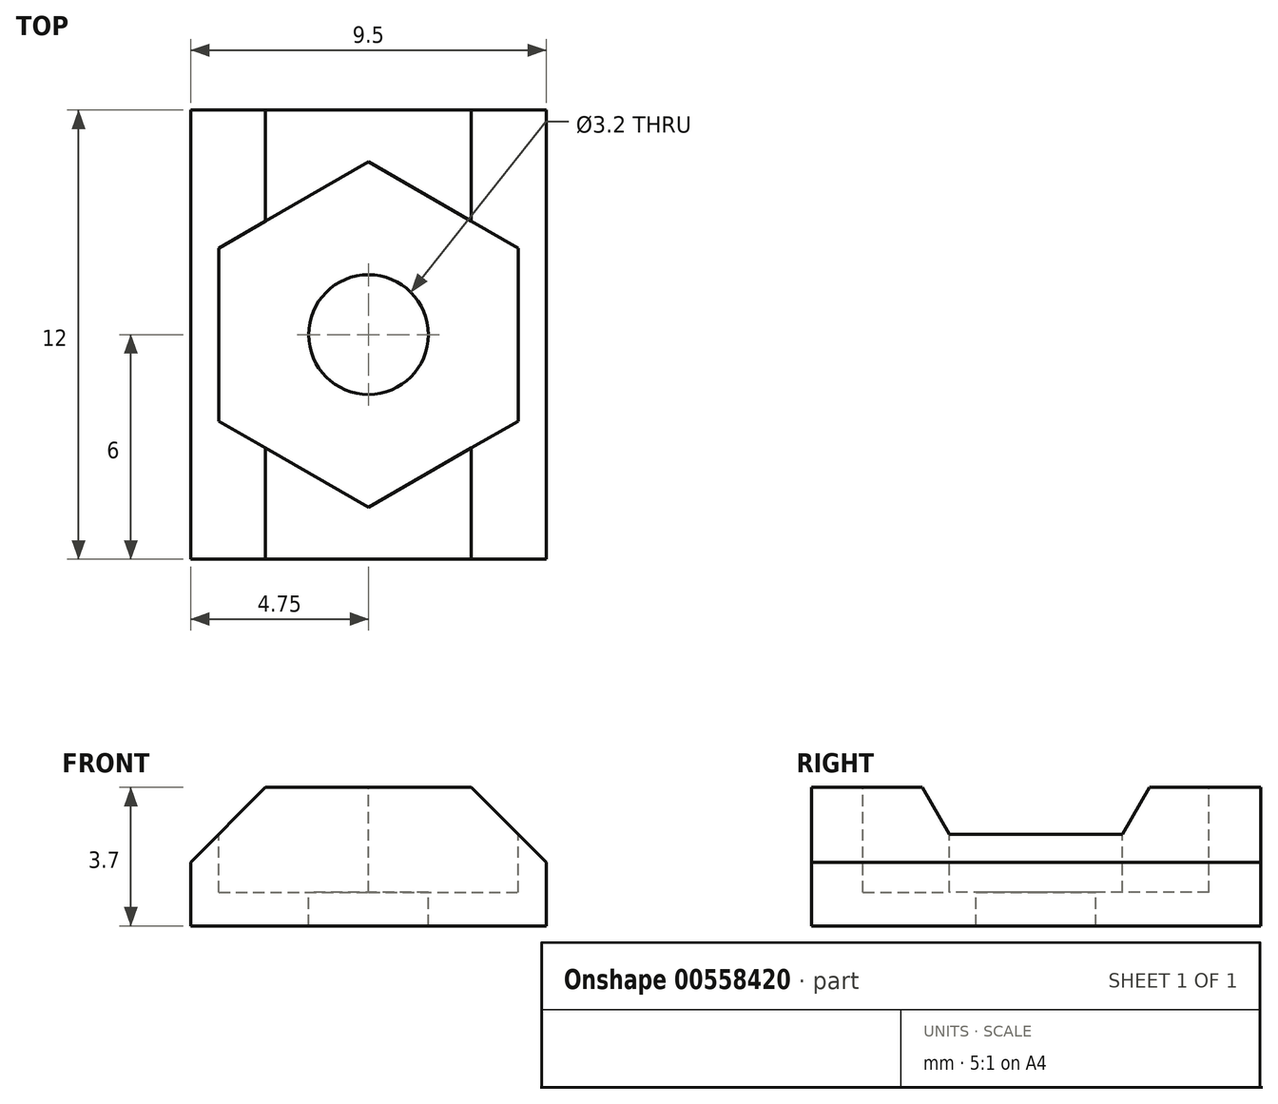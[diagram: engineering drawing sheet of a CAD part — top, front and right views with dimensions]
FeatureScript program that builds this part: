
annotation { "Feature Type Name" : "Feature", "Feature Type Description" : "" }
export const myFeature = defineFeature(function(context is Context, id is Id, definition is map)
    precondition{}
    {
        {
            var Q0;
            Q0=qCreatedBy(makeId("Front.planeOp"),FACE);
            var sketch = newSketch(context, id + "F0", { "sketchPlane" : qUnion([Q0])});
            skLineSegment(sketch, "E0", {"start": v(0, 0) * mm, "end": v(-4.75, 0) * mm});
            skLineSegment(sketch, "E1", {"start": v(0, 0) * mm, "end": v(4.75, 0) * mm});
            skLineSegment(sketch, "E2", {"start": v(4.75, 0) * mm, "end": v(4.75, 3.7) * mm});
            skLineSegment(sketch, "E3", {"start": v(4.75, 3.7) * mm, "end": v(-4.75, 3.7) * mm});
            skLineSegment(sketch, "E4", {"start": v(-4.75, 3.7) * mm, "end": v(-4.75, 0) * mm});
            skSolve(sketch);
        }
        {
            var Q0;
            Q0=qSketchRegion(id+"F0",true);
            extrude(context, id + "F1", {"entities" : qUnion([Q0]), "endBound" : BoundingType.SYMMETRIC, "depth" : 12 * mm, "offsetDistance" : 25 * mm});
        }
        {
            var Q0;
            Q0=makeQuery(id+"F1.opExtrude","SWEPT_FACE",FACE,{"disambiguationData":[OSD([sQuery(id+"F0.wireOp",EDGE,"E3")])]});
            var sketch = newSketch(context, id + "F2", { "sketchPlane" : qUnion([Q0])});
            skCircle(sketch, "E5", {"center": v(0, 0) * mm, "radius": 1.6 * mm});
            skSolve(sketch);
        }
        {
            var Q0;
            Q0=qSketchRegion(id+"F2",true);
            extrude(context, id + "F3", {"entities" : qUnion([Q0]), "operationType" : NewBodyOperationType.REMOVE, "endBound" : BoundingType.UP_TO_NEXT, "oppositeDirection" : true, "depth" : 25 * mm});
        }
        {
            var Q0;
            Q0=makeQuery(id+"F1.opExtrude","SWEPT_FACE",FACE,{"disambiguationData":[OSD([sQuery(id+"F0.wireOp",EDGE,"E3")])]});
            var sketch = newSketch(context, id + "F4", { "sketchPlane" : qUnion([Q0])});
            skCircle(sketch, "E6.cCircle", {"center": v(0, 0) * mm, "radius": 4 * mm, "construction": true});
            skLineSegment(sketch, "E6.0", {"start": v(4, 2.3) * mm, "end": v(4, -2.3) * mm});
            skLineSegment(sketch, "E6.1", {"start": v(4, -2.3) * mm, "end": v(0, -4.62) * mm});
            skLineSegment(sketch, "E6.2", {"start": v(0, -4.62) * mm, "end": v(-4, -2.3) * mm});
            skLineSegment(sketch, "E6.3", {"start": v(-4, -2.3) * mm, "end": v(-4, 2.3) * mm});
            skLineSegment(sketch, "E6.4", {"start": v(-4, 2.3) * mm, "end": v(0, 4.62) * mm});
            skLineSegment(sketch, "E6.5", {"start": v(0, 4.62) * mm, "end": v(4, 2.3) * mm});
            skPoint(sketch, "E6.0.midPoint", {"position": v(4, 0) * mm});
            skSolve(sketch);
        }
        {
            var Q0;
            Q0=makeQuery(id+"F1.opExtrude","SWEPT_EDGE",EDGE,{"disambiguationData":[OSD([sQuery(id+"F0.wireOp",EDGE,"E3"),sQuery(id+"F0.wireOp",EDGE,"E4")])]});
            var Q1;
            Q1=makeQuery(id+"F1.opExtrude","SWEPT_EDGE",EDGE,{"disambiguationData":[OSD([sQuery(id+"F0.wireOp",EDGE,"E2"),sQuery(id+"F0.wireOp",EDGE,"E3")])]});
            chamfer(context, id + "F5", {"entities" : qUnion([Q0, Q1]), "chamferType" : ChamferType.TWO_OFFSETS, "width1" : 2 * mm, "oppositeDirection" : false, "width2" : 2 * mm, "tangentPropagation" : true});
        }
        {
            var Q0;
            Q0=qSketchRegion(id+"F4",true);
            extrude(context, id + "F6", {"entities" : qUnion([Q0]), "operationType" : NewBodyOperationType.REMOVE, "oppositeDirection" : true, "depth" : 2.8 * mm, "offsetDistance" : 25 * mm});
        }
    });
